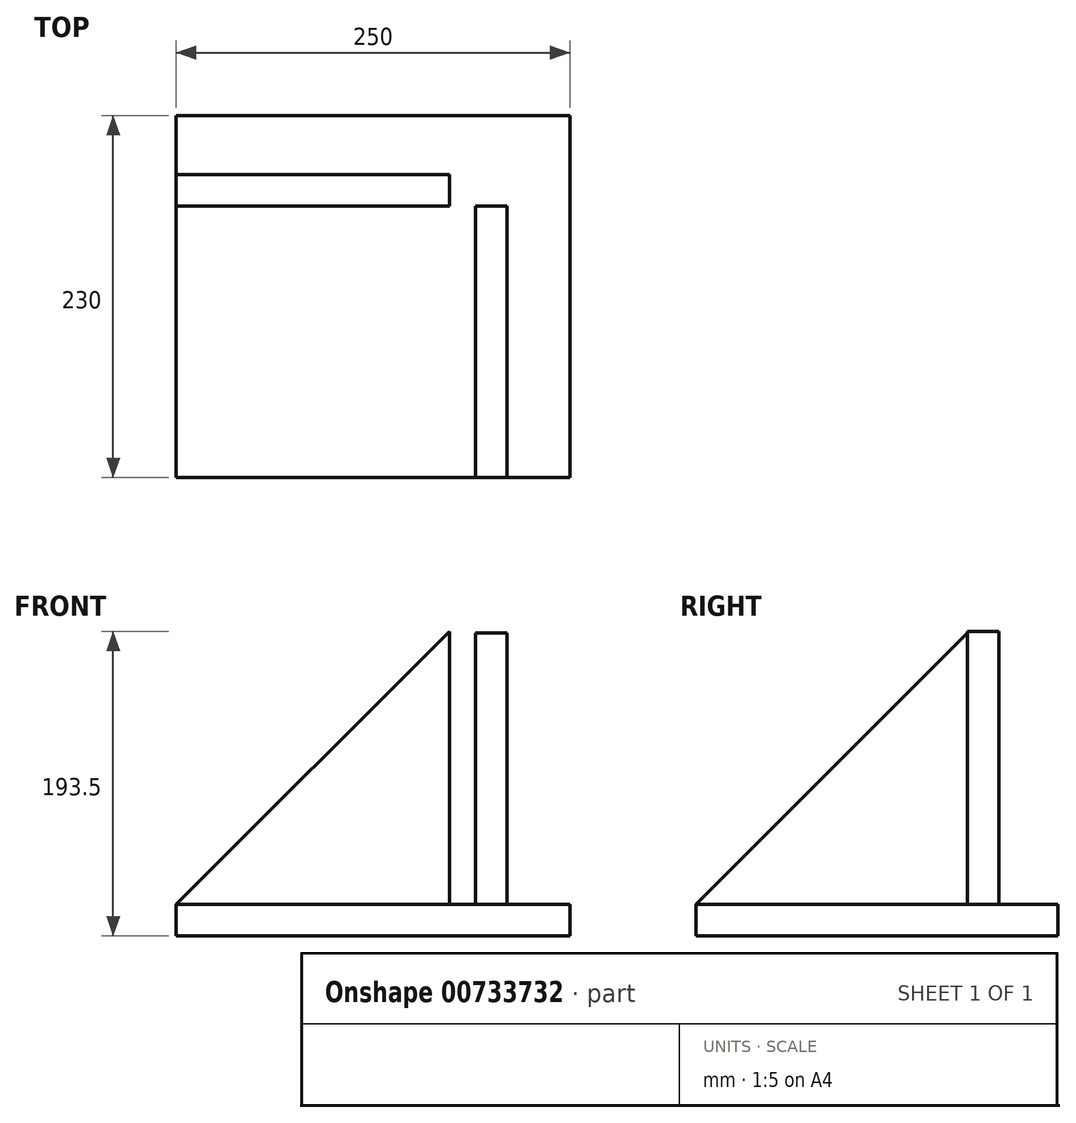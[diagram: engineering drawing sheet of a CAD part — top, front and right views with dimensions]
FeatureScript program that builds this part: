
annotation { "Feature Type Name" : "Feature", "Feature Type Description" : "" }
export const myFeature = defineFeature(function(context is Context, id is Id, definition is map)
    precondition{}
    {
        {
            var Q0;
            Q0=qCreatedBy(makeId("Top.planeOp"),FACE);
            var sketch = newSketch(context, id + "F0", { "sketchPlane" : qUnion([Q0])});
            skLineSegment(sketch, "E0.bottom", {"start": v(125, -115) * mm, "end": v(-125, -115) * mm});
            skLineSegment(sketch, "E0.top", {"start": v(125, 115) * mm, "end": v(-125, 115) * mm});
            skLineSegment(sketch, "E0.left", {"start": v(125, -115) * mm, "end": v(125, 115) * mm});
            skLineSegment(sketch, "E0.right", {"start": v(-125, -115) * mm, "end": v(-125, 115) * mm});
            skPoint(sketch, "E0.middle", {"position": v(0, 0) * mm});
            skSolve(sketch);
        }
        {
            var Q0;
            Q0=makeQuery(id+"F0.imprint","IMPRINT",FACE,{"disambiguationData":[TD([[makeQuery(id+"F0.imprint","IMPRINT",EDGE,{"derivedFrom":sQuery(id+"F0.wireOp",EDGE,"E0.bottom")}),-1.0]])]});
            extrude(context, id + "F1", {"entities" : qUnion([Q0]), "depth" : 20 * mm, "offsetDistance" : 25 * mm});
        }
        {
            var Q0;
            Q0=makeQuery(id+"F1.opExtrude","SWEPT_FACE",FACE,{"disambiguationData":[OSD([sQuery(id+"F0.wireOp",EDGE,"E0.top")])]});
            var sketch = newSketch(context, id + "F2", { "sketchPlane" : qUnion([Q0])});
            skLineSegment(sketch, "E1", {"start": v(125, 20) * mm, "end": v(-48.5, 20) * mm});
            skLineSegment(sketch, "E2", {"start": v(-48.5, 20) * mm, "end": v(-48.5, 193.5) * mm});
            skLineSegment(sketch, "E3", {"start": v(-48.5, 193.5) * mm, "end": v(125, 20) * mm});
            skSolve(sketch);
        }
        {
            var Q0;
            Q0=qSketchRegion(id+"F2",true);
            extrude(context, id + "F3", {"entities" : qUnion([Q0]), "oppositeDirection" : true, "depth" : 57.5 * mm, "offsetDistance" : 25 * mm});
        }
        {
            var Q0;
            Q0=makeQuery(id+"F3.opExtrude","CAP_FACE",FACE,{"disambiguationData":[OSD([sQuery(id+"F2.wireOp",EDGE,"E1"),sQuery(id+"F2.wireOp",EDGE,"E2"),sQuery(id+"F2.wireOp",EDGE,"E3")])],"isStart":true});
            extrude(context, id + "F4", {"entities" : qUnion([Q0]), "operationType" : NewBodyOperationType.REMOVE, "oppositeDirection" : true, "depth" : 37.5 * mm, "offsetDistance" : 25 * mm});
        }
        {
            var Q0;
            Q0=makeQuery(id+"F1.opExtrude","SWEPT_FACE",FACE,{"disambiguationData":[OSD([sQuery(id+"F0.wireOp",EDGE,"E0.left")])]});
            var sketch = newSketch(context, id + "F5", { "sketchPlane" : qUnion([Q0])});
            skLineSegment(sketch, "E4", {"start": v(-115, 20) * mm, "end": v(57.5, 20) * mm});
            skLineSegment(sketch, "E5", {"start": v(57.5, 20) * mm, "end": v(57.5, 192.5) * mm});
            skLineSegment(sketch, "E6", {"start": v(57.5, 192.5) * mm, "end": v(-115, 20) * mm});
            skSolve(sketch);
        }
        {
            var Q0;
            Q0=qSketchRegion(id+"F5",true);
            extrude(context, id + "F6", {"entities" : qUnion([Q0]), "operationType" : NewBodyOperationType.ADD, "oppositeDirection" : true, "depth" : 60 * mm, "offsetDistance" : 25 * mm});
        }
        {
            var Q0;
            Q0=makeQuery(id+"F5.imprint","IMPRINT",FACE,{"disambiguationData":[TD([[makeQuery(id+"F5.imprint","IMPRINT",EDGE,{"derivedFrom":sQuery(id+"F5.wireOp",EDGE,"E4")}),1.0]])]});
            extrude(context, id + "F7", {"entities" : qUnion([Q0]), "operationType" : NewBodyOperationType.REMOVE, "oppositeDirection" : true, "depth" : 40 * mm, "offsetDistance" : 25 * mm});
        }
    });
